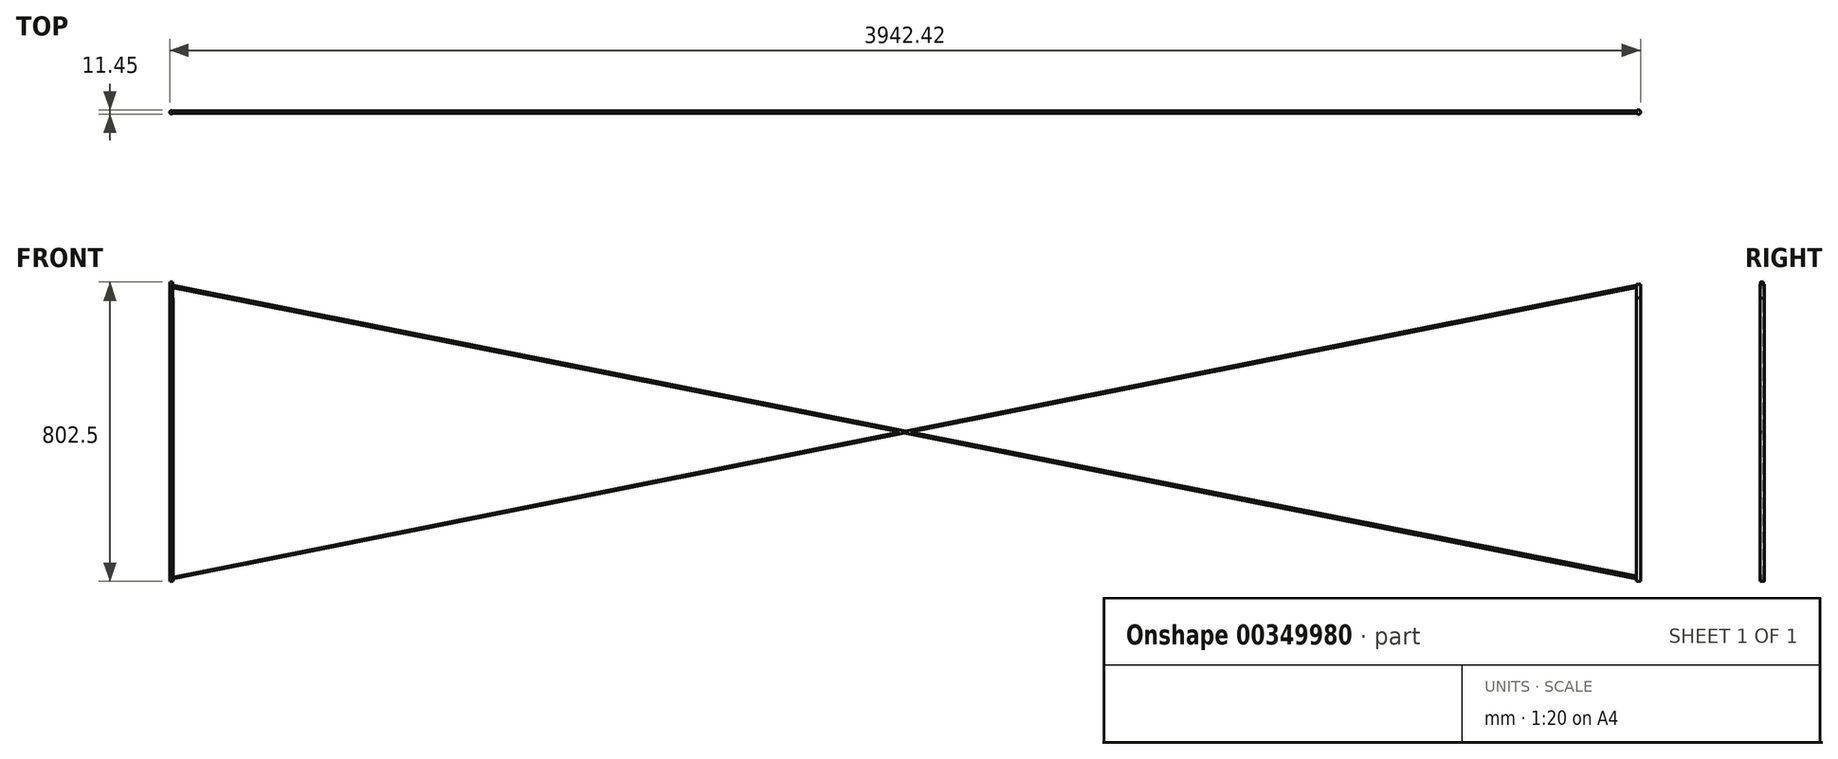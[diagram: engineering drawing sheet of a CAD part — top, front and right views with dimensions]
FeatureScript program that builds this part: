
annotation { "Feature Type Name" : "Feature", "Feature Type Description" : "" }
export const myFeature = defineFeature(function(context is Context, id is Id, definition is map)
    precondition{}
    {
        {
            var Q0;
            Q0=qCreatedBy(makeId("Front.planeOp"),FACE);
            var sketch = newSketch(context, id + "F0", { "sketchPlane" : qUnion([Q0])});
            skLineSegment(sketch, "E0", {"start": v(-3859.72, 33.8) * mm, "end": v(63.48, -746.26) * mm});
            skLineSegment(sketch, "E1", {"start": v(63.48, -746.26) * mm, "end": v(63.48, -753.37) * mm});
            skLineSegment(sketch, "E2", {"start": v(63.48, -753.37) * mm, "end": v(-3860.54, 28.18) * mm});
            skLineSegment(sketch, "E3", {"start": v(-3860.54, 28.18) * mm, "end": v(-3859.72, 33.8) * mm});
            skLineSegment(sketch, "E4", {"start": v(-3860.54, -753.37) * mm, "end": v(-3860.54, -749.1) * mm});
            skLineSegment(sketch, "E5", {"start": v(-3860.54, -749.1) * mm, "end": v(63.48, 33.8) * mm});
            skLineSegment(sketch, "E6", {"start": v(63.48, 33.8) * mm, "end": v(62.36, 28.18) * mm});
            skLineSegment(sketch, "E7", {"start": v(62.36, 28.18) * mm, "end": v(-3860.54, -753.37) * mm});
            skSolve(sketch);
        }
        {
            var Q0;
            Q0 = qSketchRegion(id + "F0", true);
            extrude(context, id + "F1", {"entities" : qUnion([Q0]), "depth" : 7 * mm, "offsetDistance" : 25 * mm});
        }
        {
            var Q0;
            Q0=qCreatedBy(makeId("Top.planeOp"),FACE);
            var sketch = newSketch(context, id + "F2", { "sketchPlane" : qUnion([Q0])});
            skCircle(sketch, "E8", {"center": v(-3863.37, -3.68) * mm, "radius": 4.39 * mm});
            skCircle(sketch, "E9", {"center": v(68.94, -3.27) * mm, "radius": 5.72 * mm});
            skSolve(sketch);
        }
        {
            var Q0;
            Q0 = qSketchRegion(id + "F2", true);
            extrude(context, id + "F3", {"entities" : qUnion([Q0]), "operationType" : NewBodyOperationType.ADD, "oppositeDirection" : true, "depth" : 760 * mm, "offsetDistance" : 25 * mm});
        }
        {
            var Q0;
            Q0=makeQuery(id+"F3.opExtrude","CAP_FACE",FACE,{"disambiguationData":[OSD([sQuery(id+"F2.wireOp",EDGE,"E8")])],"isStart":true});
            var sketch = newSketch(context, id + "F4", { "sketchPlane" : qUnion([Q0])});
            skCircle(sketch, "E10", {"center": v(-3863.37, -3.68) * mm, "radius": 4.04 * mm});
            skSolve(sketch);
        }
        {
            var Q0;
            Q0 = qSketchRegion(id + "F4", true);
            extrude(context, id + "F5", {"entities" : qUnion([Q0]), "operationType" : NewBodyOperationType.ADD, "depth" : 42.5 * mm, "offsetDistance" : 25 * mm});
        }
        {
            var Q0;
            Q0=makeQuery(id+"F3.opExtrude","CAP_FACE",FACE,{"disambiguationData":[OSD([sQuery(id+"F2.wireOp",EDGE,"E9")])],"isStart":true});
            var sketch = newSketch(context, id + "F6", { "sketchPlane" : qUnion([Q0])});
            skCircle(sketch, "E11", {"center": v(68.94, -3.27) * mm, "radius": 5.64 * mm});
            skSolve(sketch);
        }
        {
            var Q0;
            Q0 = qSketchRegion(id + "F6", true);
            extrude(context, id + "F7", {"entities" : qUnion([Q0]), "operationType" : NewBodyOperationType.ADD, "depth" : 36.4 * mm, "offsetDistance" : 25 * mm});
        }
    });
